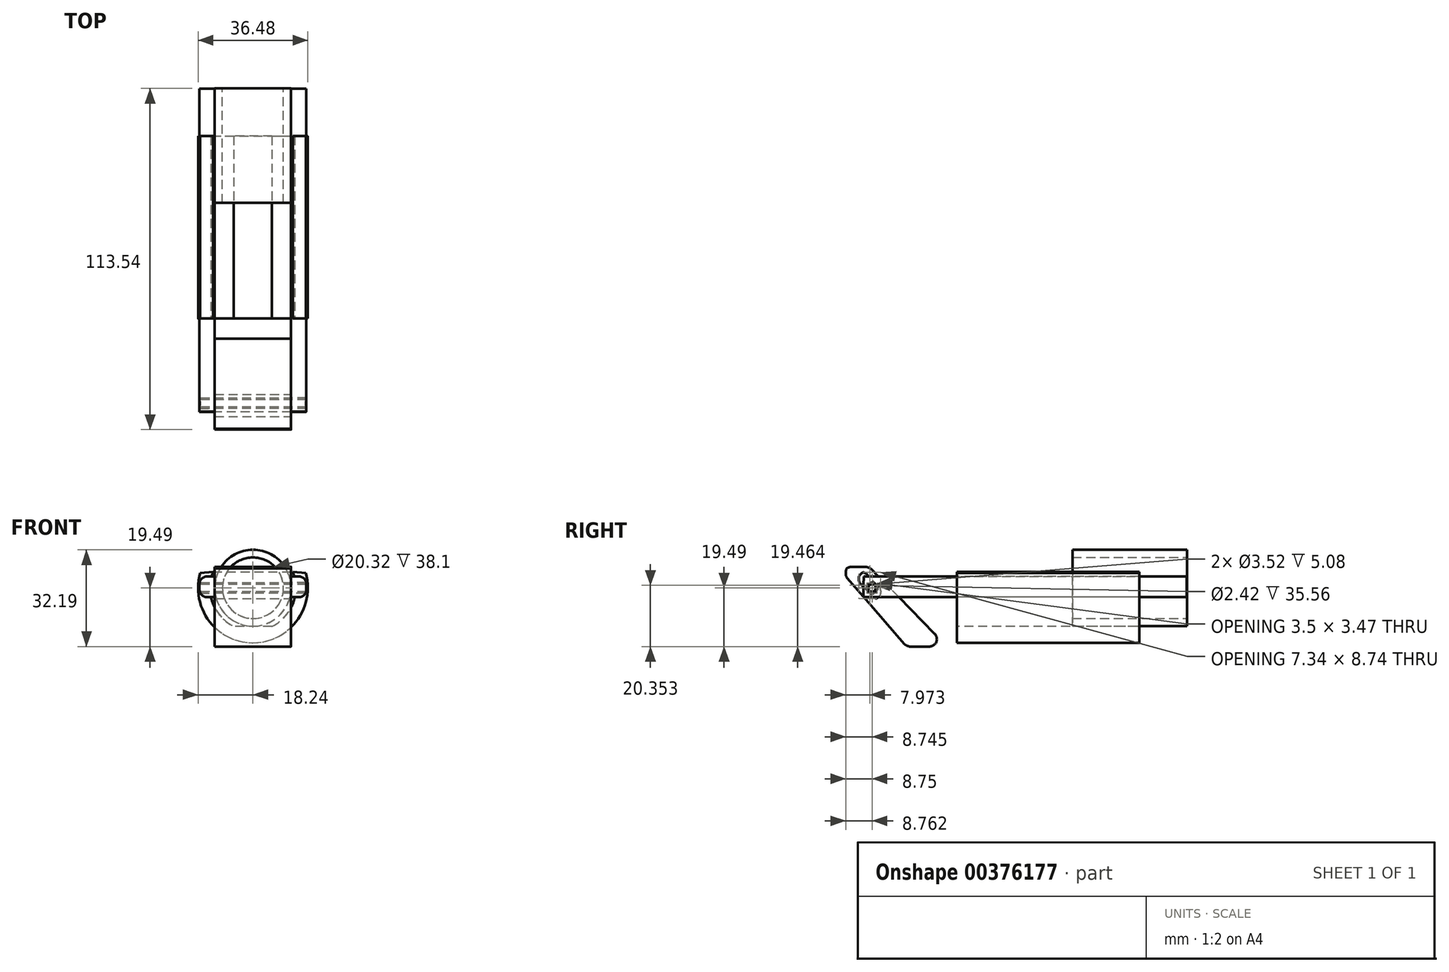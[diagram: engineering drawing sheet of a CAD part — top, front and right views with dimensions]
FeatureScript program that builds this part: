
annotation { "Feature Type Name" : "Feature", "Feature Type Description" : "" }
export const myFeature = defineFeature(function(context is Context, id is Id, definition is map)
    precondition{}
    {
        {
            var Q0;
            Q0=qCreatedBy(makeId("Right.planeOp"),FACE);
            var sketch = newSketch(context, id + "F0", { "sketchPlane" : qUnion([Q0])});
            skCircle(sketch, "E0", {"center": v(-32.91, 0) * mm, "radius": 1.82 * mm});
            skLineSegment(sketch, "E1", {"start": v(71.89, -12.7) * mm, "end": v(71.89, 12.7) * mm});
            skLineSegment(sketch, "E2", {"start": v(71.89, 12.7) * mm, "end": v(33.79, 12.7) * mm});
            skLineSegment(sketch, "E3", {"start": v(33.79, -12.7) * mm, "end": v(71.89, -12.7) * mm});
            skLineSegment(sketch, "E4", {"start": v(33.79, 12.7) * mm, "end": v(33.79, -12.7) * mm});
            skSolve(sketch);
        }
        {
            var Q0;
            {var subQ4=sQuery(id+"F0.wireOp",EDGE,"E1");Q0=makeQuery(id+"F0.imprint","IMPRINT",FACE,{"disambiguationData":[TD([[makeQuery(id+"F0.imprint","IMPRINT",EDGE,{"derivedFrom":subQ4}),1.0]])]});}
            extrude(context, id + "F1", {"entities" : qUnion([Q0]), "endBound" : BoundingType.SYMMETRIC, "depth" : 25.4 * mm});
        }
        {
            var Q0;
            Q0=makeQuery(id+"F1.opExtrude","CAP_EDGE",EDGE,{"disambiguationData":[OSD([sQuery(id+"F0.wireOp",EDGE,"E2")])],"isStart":false});
            var Q1;
            Q1=makeQuery(id+"F1.opExtrude","CAP_EDGE",EDGE,{"disambiguationData":[OSD([sQuery(id+"F0.wireOp",EDGE,"E2")])],"isStart":true});
            var Q2;
            Q2=makeQuery(id+"F1.opExtrude","CAP_EDGE",EDGE,{"disambiguationData":[OSD([sQuery(id+"F0.wireOp",EDGE,"E3")])],"isStart":false});
            var Q3;
            Q3=makeQuery(id+"F1.opExtrude","CAP_EDGE",EDGE,{"disambiguationData":[OSD([sQuery(id+"F0.wireOp",EDGE,"E3")])],"isStart":true});
            fillet(context, id + "F2", {"entities" : qUnion([Q0, Q1, Q2, Q3]), "radius" : 12.7 * mm, "tangentPropagation" : true, "allowEdgeOverflow" : false});
        }
        {
            var Q0;
            Q0=makeQuery(id+"F1.opExtrude","SWEPT_FACE",FACE,{"disambiguationData":[OSD([sQuery(id+"F0.wireOp",EDGE,"E1")])]});
            var Q1;
            Q1=makeQuery(id+"F1.opExtrude","SWEPT_FACE",FACE,{"disambiguationData":[OSD([sQuery(id+"F0.wireOp",EDGE,"E4")])]});
            shell(context, id + "F3", {"entities" : qUnion([Q0, Q1]), "thickness" : 2.54 * mm});
        }
        {
            var Q0;
            Q0=qCreatedBy(makeId("Right.planeOp"),FACE);
            var sketch = newSketch(context, id + "F4", { "sketchPlane" : qUnion([Q0])});
            skLineSegment(sketch, "E5", {"start": v(-35.7, 3.86) * mm, "end": v(71.74, 3.86) * mm});
            skLineSegment(sketch, "E6", {"start": v(71.74, 3.86) * mm, "end": v(71.74, -3.06) * mm});
            skLineSegment(sketch, "E7", {"start": v(71.74, -3.06) * mm, "end": v(-35.8, -3.06) * mm});
            skLineSegment(sketch, "E8", {"start": v(-35.8, -3.06) * mm, "end": v(-35.7, 3.86) * mm});
            skCircle(sketch, "E9", {"center": v(-32.9, 0) * mm, "radius": 1.76 * mm});
            skSolve(sketch);
        }
        {
            var Q0;
            Q0=makeQuery(id+"F4.imprint","IMPRINT",FACE,{"disambiguationData":[TD([[makeQuery(id+"F4.imprint","IMPRINT",EDGE,{"derivedFrom":sQuery(id+"F4.wireOp",EDGE,"E5")}),-1.0]])]});
            extrude(context, id + "F5", {"entities" : qUnion([Q0]), "depth" : 17.78 * mm, "hasSecondDirection" : true, "secondDirectionOppositeDirection" : false, "secondDirectionDepth" : 12.7 * mm});
        }
        {
            var Q0;
            Q0=makeQuery(id+"F5.opExtrude","CAP_EDGE",EDGE,{"disambiguationData":[OSD([sQuery(id+"F4.wireOp",EDGE,"E5")])],"isStart":false});
            var Q1;
            Q1=makeQuery(id+"F5.opExtrude","CAP_EDGE",EDGE,{"disambiguationData":[OSD([sQuery(id+"F4.wireOp",EDGE,"E7")])],"isStart":false});
            var Q2;
            {var subQ0=sQuery(id+"F4.wireOp",EDGE,"E6");var subQ1=sQuery(id+"F4.wireOp",EDGE,"E5");Q2=makeQuery(id+"FwQ0XXT8Idl5O0i_4.opExtrude","SWEPT_EDGE",EDGE,{"disambiguationData":[OSD([subQ1,subQ0]),TDD([makeQuery(id+"F5.opExtrude","CAP_VERTEX",VERTEX,{"disambiguationData":[OSD([subQ1,subQ0])],"isStart":false})])]});}
            var Q3;
            {var subQ0=sQuery(id+"F4.wireOp",EDGE,"E7");var subQ1=sQuery(id+"F4.wireOp",EDGE,"E6");Q3=makeQuery(id+"FwQ0XXT8Idl5O0i_4.opExtrude","SWEPT_EDGE",EDGE,{"disambiguationData":[OSD([subQ1,subQ0]),TDD([makeQuery(id+"F5.opExtrude","CAP_VERTEX",VERTEX,{"disambiguationData":[OSD([subQ1,subQ0])],"isStart":false})])]});}
            fillet(context, id + "F6", {"entities" : qUnion([Q0, Q1, Q2, Q3]), "radius" : 2.54 * mm, "tangentPropagation" : true, "allowEdgeOverflow" : false});
        }
        {
            var Q0;
            Q0=makeQuery(id+"F5.opExtrude","SWEPT_BODY",BODY,{"disambiguationData":[OSD([sQuery(id+"F4.wireOp",EDGE,"E5"),sQuery(id+"F4.wireOp",EDGE,"E6"),sQuery(id+"F4.wireOp",EDGE,"E7"),sQuery(id+"F4.wireOp",EDGE,"E8"),sQuery(id+"F4.wireOp",EDGE,"E9")])]});
            var Q1;
            Q1=qCreatedBy(makeId("Right.planeOp"),FACE);
            mirror(context, id + "F7", {"operationType" : NewBodyOperationType.ADD, "entities" : qUnion([Q0]), "mirrorPlane" : qUnion([Q1])});
        }
        {
            var Q0;
            Q0=qCreatedBy(makeId("Right.planeOp"),FACE);
            var sketch = newSketch(context, id + "F8", { "sketchPlane" : qUnion([Q0])});
            skLineSegment(sketch, "E10", {"start": v(-7.9, -19.49) * mm, "end": v(-33.87, 7.01) * mm});
            skLineSegment(sketch, "E11", {"start": v(-21.48, -19.49) * mm, "end": v(-7.9, -19.49) * mm});
            skPoint(sketch, "E12", {"position": v(-33.2, 0) * mm});
            skLineSegment(sketch, "E13", {"start": v(-26.58, -3.7) * mm, "end": v(-35.54, 5.43) * mm});
            skLineSegment(sketch, "E14", {"start": v(-35.54, 5.43) * mm, "end": v(-40.77, 5.43) * mm});
            skLineSegment(sketch, "E15", {"start": v(-40.77, 5.43) * mm, "end": v(-31.82, -3.7) * mm});
            skLineSegment(sketch, "E16", {"start": v(-31.82, -3.7) * mm, "end": v(-26.58, -3.7) * mm});
            skLineSegment(sketch, "E17", {"start": v(-21.48, -19.49) * mm, "end": v(-42.81, 5.22) * mm});
            skLineSegment(sketch, "E18", {"start": v(-42.81, 5.22) * mm, "end": v(-40.92, 7.01) * mm});
            skLineSegment(sketch, "E19", {"start": v(-40.92, 7.01) * mm, "end": v(-33.87, 7.01) * mm});
            skSolve(sketch);
        }
        {
            var Q0;
            Q0=qSketchRegion(id+"F8",true);
            extrude(context, id + "F9", {"entities" : qUnion([Q0]), "endBound" : BoundingType.SYMMETRIC, "depth" : 25.4 * mm});
        }
        {
            var Q0;
            Q0=makeQuery(id+"F9.opExtrude","SWEPT_EDGE",EDGE,{"disambiguationData":[OSD([sQuery(id+"F8.wireOp",EDGE,"E13"),sQuery(id+"F8.wireOp",EDGE,"E16")])]});
            var Q1;
            Q1=makeQuery(id+"F9.opExtrude","SWEPT_EDGE",EDGE,{"disambiguationData":[OSD([sQuery(id+"F8.wireOp",EDGE,"E15"),sQuery(id+"F8.wireOp",EDGE,"E16")])]});
            var Q2;
            Q2=makeQuery(id+"F9.opExtrude","SWEPT_EDGE",EDGE,{"disambiguationData":[OSD([sQuery(id+"F8.wireOp",EDGE,"E13"),sQuery(id+"F8.wireOp",EDGE,"E14")])]});
            var Q3;
            Q3=makeQuery(id+"F9.opExtrude","SWEPT_EDGE",EDGE,{"disambiguationData":[OSD([sQuery(id+"F8.wireOp",EDGE,"E14"),sQuery(id+"F8.wireOp",EDGE,"E15")])]});
            fillet(context, id + "F10", {"entities" : qUnion([Q0, Q1, Q2, Q3]), "radius" : 2.54 * mm, "tangentPropagation" : true, "rho" : 0.3, "crossSection" : FilletCrossSection.CONIC, "allowEdgeOverflow" : false});
        }
        {
            var Q0;
            Q0=makeQuery(id+"F9.opExtrude","SWEPT_EDGE",EDGE,{"disambiguationData":[OSD([sQuery(id+"F8.wireOp",EDGE,"E18"),sQuery(id+"F8.wireOp",EDGE,"E19")])]});
            var Q1;
            Q1=makeQuery(id+"F9.opExtrude","SWEPT_EDGE",EDGE,{"disambiguationData":[OSD([sQuery(id+"F8.wireOp",EDGE,"E17"),sQuery(id+"F8.wireOp",EDGE,"E18")])]});
            var Q2;
            Q2=makeQuery(id+"F9.opExtrude","SWEPT_EDGE",EDGE,{"disambiguationData":[OSD([sQuery(id+"F8.wireOp",EDGE,"E10"),sQuery(id+"F8.wireOp",EDGE,"E19")])]});
            var Q3;
            Q3=makeQuery(id+"F9.opExtrude","SWEPT_EDGE",EDGE,{"disambiguationData":[OSD([sQuery(id+"F8.wireOp",EDGE,"E11"),sQuery(id+"F8.wireOp",EDGE,"E17")])]});
            var Q4;
            Q4=makeQuery(id+"F9.opExtrude","SWEPT_EDGE",EDGE,{"disambiguationData":[OSD([sQuery(id+"F8.wireOp",EDGE,"E10"),sQuery(id+"F8.wireOp",EDGE,"E11")])]});
            fillet(context, id + "F11", {"entities" : qUnion([Q0, Q1, Q2, Q3, Q4]), "radius" : 2.54 * mm, "tangentPropagation" : true, "rho" : 0.3, "crossSection" : FilletCrossSection.CONIC, "allowEdgeOverflow" : false});
        }
        {
            var Q0;
            Q0=qCreatedBy(makeId("Right.planeOp"),FACE);
            var sketch = newSketch(context, id + "F12", { "sketchPlane" : qUnion([Q0])});
            skLineSegment(sketch, "E20", {"start": v(-4.67, -17.1) * mm, "end": v(56.02, -17.1) * mm});
            skLineSegment(sketch, "E21", {"start": v(56.02, -17.1) * mm, "end": v(56.02, -12.8) * mm});
            skLineSegment(sketch, "E22", {"start": v(56.02, -12.8) * mm, "end": v(-4.67, -12.8) * mm});
            skLineSegment(sketch, "E23", {"start": v(-4.67, -12.8) * mm, "end": v(-4.67, -17.1) * mm});
            skPoint(sketch, "E24.centerSnap0", {"position": v(-4.67, -14.95) * mm});
            skSolve(sketch);
        }
        {
            var Q0;
            Q0=makeQuery(id+"F12.imprint","IMPRINT",FACE,{"disambiguationData":[TD([[makeQuery(id+"F12.imprint","IMPRINT",EDGE,{"derivedFrom":sQuery(id+"F12.wireOp",EDGE,"E20")}),1.0]])]});
            var Q1;
            Q1 = qSketchRegion(id + "F12", true);
            extrude(context, id + "F13", {"entities" : qUnion([Q0, Q1]), "operationType" : NewBodyOperationType.ADD, "endBound" : BoundingType.SYMMETRIC, "depth" : 12.7 * mm});
        }
        {
            var Q0;
            Q0=makeQuery(id+"F13.opExtrude","CAP_FACE",FACE,{"disambiguationData":[OSD([sQuery(id+"F12.wireOp",EDGE,"E20"),sQuery(id+"F12.wireOp",EDGE,"E21"),sQuery(id+"F12.wireOp",EDGE,"E22"),sQuery(id+"F12.wireOp",EDGE,"E23"),sQuery(id+"F12.wireOp",EDGE,"E24")])],"isStart":false});
            var Q1;
            Q1=makeQuery(id+"F13.opExtrude","CAP_FACE",FACE,{"disambiguationData":[OSD([sQuery(id+"F12.wireOp",EDGE,"E20"),sQuery(id+"F12.wireOp",EDGE,"E21"),sQuery(id+"F12.wireOp",EDGE,"E22"),sQuery(id+"F12.wireOp",EDGE,"E23"),sQuery(id+"F12.wireOp",EDGE,"E24")])],"isStart":true});
            var Q2;
            Q2=makeQuery(id+"F2.opFillet","BLEND_FACE",FACE,{"disambiguationData":[OSD([sQuery(id+"F0.wireOp",EDGE,"E2")])]});
            revolve(context, id + "F14", {"operationType" : NewBodyOperationType.ADD, "entities" : qUnion([Q0, Q1]), "axis" : qUnion([Q2]), "revolveType" : RevolveType.SYMMETRIC, "angle" : 171 * degree});
        }
        {
            var Q0;
            Q0=qCreatedBy(makeId("Right.planeOp"),FACE);
            var sketch = newSketch(context, id + "F15", { "sketchPlane" : qUnion([Q0])});
            skCircle(sketch, "E25", {"center": v(-32.89, 0) * mm, "radius": 1.73 * mm});
            skCircle(sketch, "E26", {"center": v(-32.89, 0) * mm, "radius": 1.21 * mm});
            skSolve(sketch);
        }
        {
            var Q0;
            Q0 = qSketchRegion(id + "F15", true);
            extrude(context, id + "F16", {"entities" : qUnion([Q0]), "endBound" : BoundingType.SYMMETRIC, "depth" : 35.56 * mm});
        }
    });
